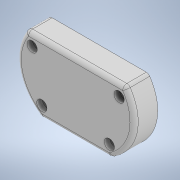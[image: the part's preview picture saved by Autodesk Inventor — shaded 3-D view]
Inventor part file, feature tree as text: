
AUTODESK INVENTOR PART (.ipt)
format: ipt  version: 2021 (Build 250183000, 183)  size: 1,035,264 bytes
history: native  units: mm
features: sketch x8, reference x8, move_body x8, extrude x7, fillet x4, other x3, delete_face x2, direct_edit x2, hole x1
ambient origin geometry x8: Origin, YZ Plane, XZ Plane, XY Plane, X Axis, Y Axis, Z Axis, Center Point
bodies: Volumenkörper1 (feature_tree)
feature tree (43):
  extrude  "Extrusion1"  Depth=4.0mm TaperAngle=0.0deg
  delete_face  "Fläche löschen1"
  direct_edit  "Direktbearbeitung2"
  extrude  "Extrusion3"  TaperAngle=0.0deg  [1 undecoded]
  extrude  "Extrusion4"  Depth=4.0mm
  delete_face  "Fläche löschen2"
  fillet  "Rundung1"  Radius=12.0mm
  fillet  "Rundung2"  Radius=23.0mm
  extrude  "Extrusion5"  Depth=32.9mm
  hole  "Bohrung1"  [1 undecoded]
  fillet  "Rundung3"  Radius=2.0mm
  direct_edit  "Direktbearbeitung3"
  extrude  "Extrusion7"  TaperAngle=0.0deg  [1 undecoded]
  fillet  "Rundung5"  [1 undecoded]
  extrude  "Extrusion8"  TaperAngle=0.0deg  [1 undecoded]
  extrude  "Extrusion9"  TaperAngle=0.0deg  [1 undecoded]
  sketch  "Skizze1"  dims[d0=23.0mm d1=0.0mm d16=0.0mm d17=0.0mm d18=4.0mm]
  reference  "Referenz1"
  reference  "Referenz2"
  sketch  "Skizze4"  dims[d19=4.0mm d20=0.0mm d21=0.0mm d22=-4.0mm d23=0.0mm d24=0.0mm]
  sketch  "Skizze5"  dims[d25=0.0mm d26=0.0mm d27=4.0mm d28=12.0mm d29=12.0mm d30=23.0mm d31=0.0mm]
  reference  "Referenz3"
  reference  "Referenz4"
  reference  "Referenz5"
  reference  "Referenz6"
  reference  "Referenz7"
  reference  "Referenz8"
  sketch  "Skizze6"  dims[d34=42.5mm d35=32.9mm]
  sketch  "Skizze7"  dims[d37=5.0mm d38=0.0mm d39=2.0mm d40=2.0mm]
  sketch  "Skizze9"  dims[d41=6.0mm d42=0.0mm]
  sketch  "Skizze10"  dims[d43=5.5mm d44=6.0mm d45=10.0mm d46=5.4mm d47=90.0deg d48=17.8mm d49=0.0mm d50=0.0mm d51=0.0mm]
  sketch  "Skizze11"  dims[d52=0.0mm d53=0.0mm d54=0.0mm d55=0.0mm d56=0.0mm d57=0.0mm d58=4.0mm d59=-0.25mm d60=0.0mm d61=0.0mm d62=0.0mm d63=0.0mm d64=-0.25mm d65=0.25mm d66=0.0mm d67=0.0mm d68=0.0mm d69=0.0mm d70=-0.25mm d78=14.0mm d79=10.0mm d80=13.6mm d81=3.0mm d82=87.75mm d83=0.0mm d84=4.0mm d85=4.0mm d86=4.0mm d87=33.0mm d88=33.0mm d89=5.0mm d90=31.0mm d91=3.0mm d92=0.0mm d93=1.6mm d94=1.6mm d95=6.0mm d96=0.0mm d71=0.5mm d72=0.872665mm d73=0.5mm d74=0.872665mm]
  other  "Bionic_Hand_Baugruppe_Version_1.iam"
  other  "Unterarm_Teil_2:1"
  other  "Unterarm_Teil_1:1"
  move_body  "Verschieben5"
  move_body  "Verschieben6"
  move_body  "Verschieben7"
  move_body  "Verschieben8"
  move_body  "Verschieben9"
  move_body  "Verschieben10"
  move_body  "Verschieben11"
  move_body  "Verschieben12"
note: 6 required parameter values undecoded (feature->parameter linkage not recoverable at this tier; creation-order binding heuristic only, values carry confidence <= 0.55)
